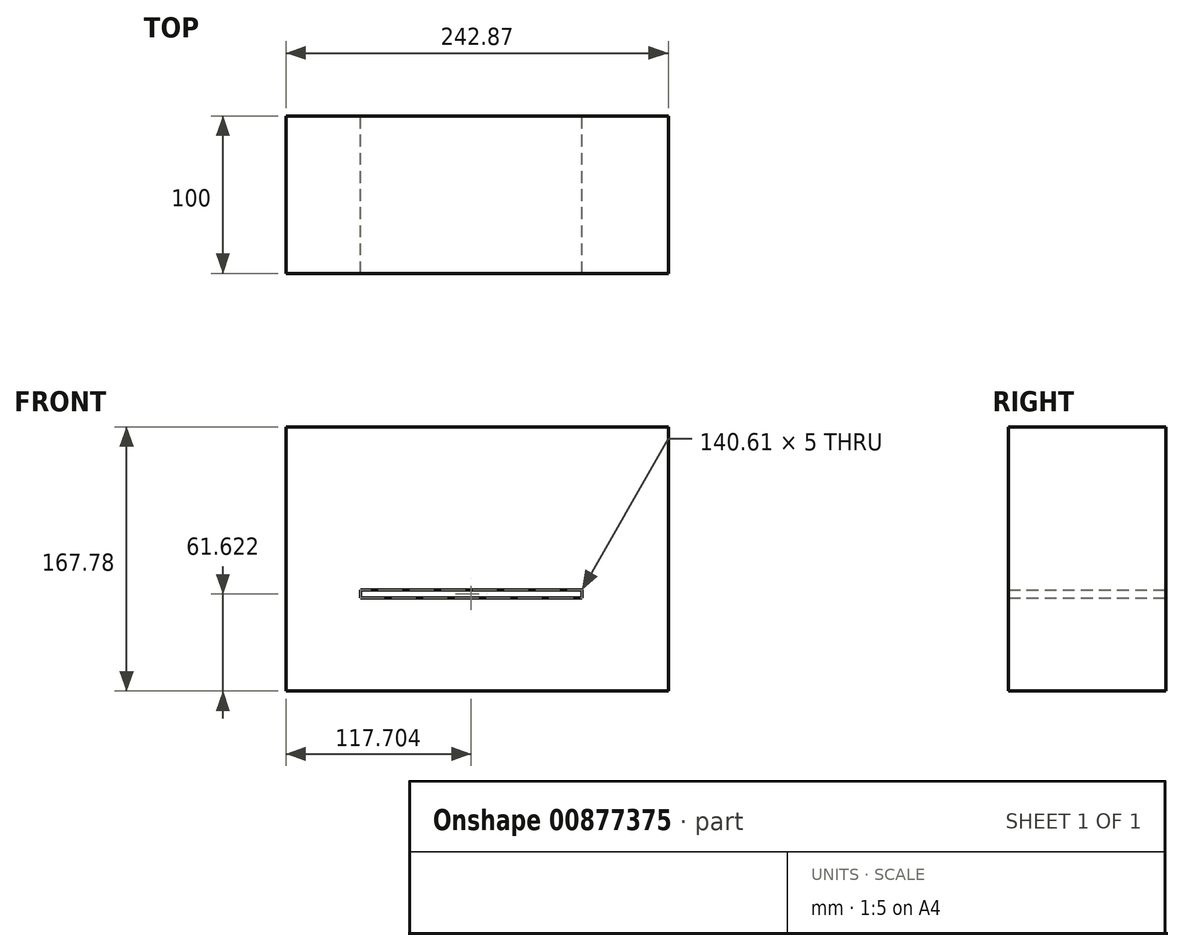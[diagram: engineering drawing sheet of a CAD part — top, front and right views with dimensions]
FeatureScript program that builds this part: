
annotation { "Feature Type Name" : "Feature", "Feature Type Description" : "" }
export const myFeature = defineFeature(function(context is Context, id is Id, definition is map)
    precondition{}
    {
        {
            var Q0;
            Q0=qCreatedBy(makeId("Front.planeOp"),FACE);
            var sketch = newSketch(context, id + "F0", { "sketchPlane" : qUnion([Q0])});
            skLineSegment(sketch, "E0.bottom", {"start": v(-108.5, 80.47) * mm, "end": v(134.38, 80.47) * mm});
            skLineSegment(sketch, "E0.top", {"start": v(-108.5, -87.3) * mm, "end": v(134.38, -87.3) * mm});
            skLineSegment(sketch, "E0.left", {"start": v(-108.5, 80.47) * mm, "end": v(-108.5, -87.3) * mm});
            skLineSegment(sketch, "E0.right", {"start": v(134.38, 80.47) * mm, "end": v(134.38, -87.3) * mm});
            skLineSegment(sketch, "E1", {"start": v(-9.43, 80.47) * mm, "end": v(-9.43, -13.8) * mm});
            skLineSegment(sketch, "E2", {"start": v(-61.1, -13.8) * mm, "end": v(-61.1, -87.3) * mm});
            skLineSegment(sketch, "E3", {"start": v(-61.1, -28.19) * mm, "end": v(79.52, -28.19) * mm});
            skLineSegment(sketch, "E4", {"start": v(79.52, 80.47) * mm, "end": v(79.52, -28.19) * mm});
            skLineSegment(sketch, "E5", {"start": v(79.52, 0) * mm, "end": v(134.38, 0) * mm});
            skLineSegment(sketch, "E6", {"start": v(39.04, -28.19) * mm, "end": v(39.04, -87.3) * mm});
            skLineSegment(sketch, "E7", {"start": v(219.6, 92.18) * mm, "end": v(219.6, 99.1) * mm});
            skLineSegment(sketch, "E8.0", {"start": v(-61.1, -23.19) * mm, "end": v(79.52, -23.19) * mm});
            skLineSegment(sketch, "E9.0", {"start": v(34.04, -28.19) * mm, "end": v(34.04, -87.3) * mm});
            skLineSegment(sketch, "E10.0", {"start": v(-56.1, -13.8) * mm, "end": v(-56.1, -87.3) * mm});
            skSolve(sketch);
        }
        {
            var Q0;
            Q0 = qSketchRegion(id + "F0", true);
            extrude(context, id + "F1", {"entities" : qUnion([Q0]), "depth" : 100 * mm, "offsetDistance" : 25 * mm});
        }
        {
            var Q0;
            {var subQ0=sQuery(id+"F0.wireOp",EDGE,"E9.0");Q0=makeQuery(id+"F0.imprint","IMPRINT",FACE,{"disambiguationData":[TD([[makeQuery(id+"F0.imprint","IMPRINT",EDGE,{"derivedFrom":subQ0}),-1.0]])]});}
            extrude(context, id + "F2", {"entities" : qUnion([Q0]), "operationType" : NewBodyOperationType.REMOVE, "oppositeDirection" : true, "depth" : 90 * mm, "offsetDistance" : 25 * mm});
        }
    });
